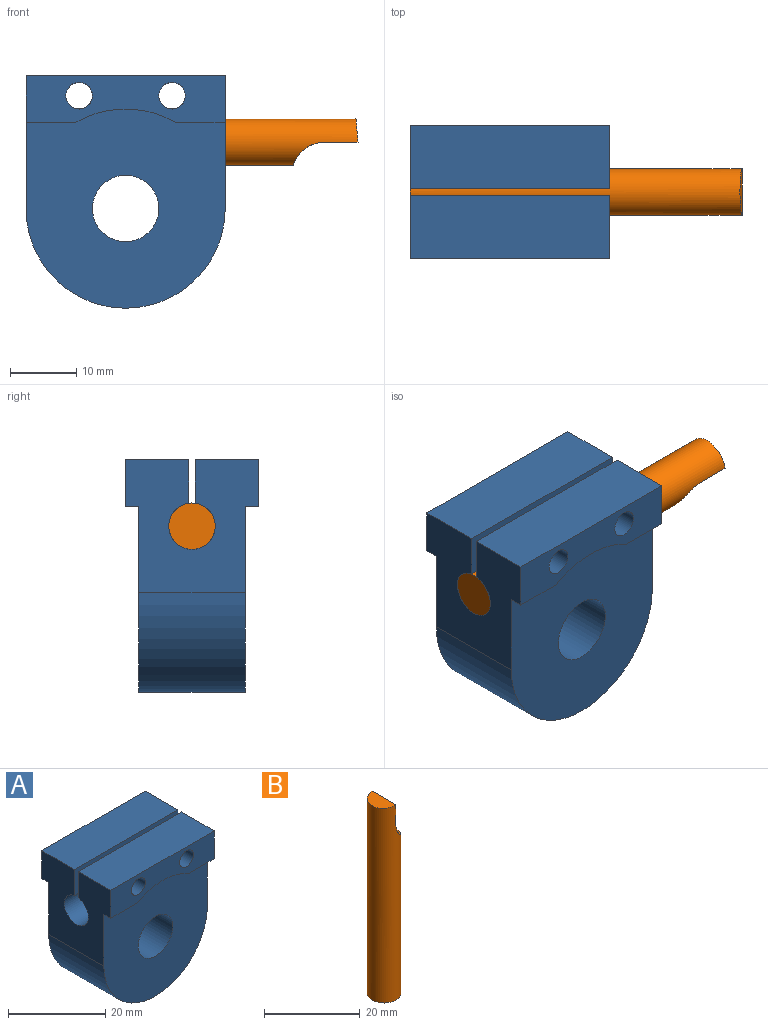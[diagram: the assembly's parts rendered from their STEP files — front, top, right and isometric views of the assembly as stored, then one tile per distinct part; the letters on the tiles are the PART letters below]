
ASSEMBLY  parts=2 mates=1
PART A: 23 faces, bbox 30x20x35 mm
  f0: cylinder r=5mm len=16mm, axis (0,1,0), area 502.7mm2, adj f18,f22
  f1: plane 20x20mm, normal (-1,0,0), area 303mm2, adj f3,f4,f5,f10,f11,f12,f13,f14
  f2: plane 20x20mm, normal (1,0,0), area 303mm2, adj f3,f4,f5,f10,f11,f12,f13,f14
  f3: cylinder r=15mm len=30mm, axis (0,1,0), area 754mm2, adj f1,f2,f18,f22
  f4: plane 30x7mm, normal (0,-1,0), area 164.6mm2, adj f1,f2,f5,f7,f9,f19,f20,f21
  f5: plane 30x9.5mm, normal (0,0,1), area 285mm2, adj f1,f2,f4,f14
  f6: cylinder r=2mm len=9.5mm, axis (0,1,0), area 119.4mm2, adj f11,f13
  f7: cylinder r=2mm len=9.5mm, axis (0,1,0), area 119.4mm2, adj f4,f14
  f8: cylinder r=2mm len=9.5mm, axis (0,1,0), area 119.4mm2, adj f11,f13
  f9: cylinder r=2mm len=9.5mm, axis (0,1,0), area 119.4mm2, adj f4,f14
  f10: plane 30x9.5mm, normal (0,0,1), area 285mm2, adj f1,f2,f11,f13
  f11: plane 30x7mm, normal (0,1,0), area 164.6mm2, adj f1,f2,f6,f8,f10,f15,f16,f17
  f12: cylinder r=3.5mm len=30mm, axis (1,0,0), area 629.6mm2, adj f1,f2,f13,f14
  f13: plane 30x6.54mm, normal (0,-1,0), area 170.9mm2, adj f1,f2,f6,f8,f10,f12
  f14: plane 30x6.54mm, normal (0,1,0), area 170.9mm2, adj f1,f2,f5,f7,f9,f12
  f15: plane 7.52x2mm, normal (0,0,-1), area 15mm2, adj f2,f11,f17,f18
  f16: plane 7.52x2mm, normal (0,0,-1), area 15mm2, adj f1,f11,f17,f18
  f17: cylinder r=15mm len=14.97mm, axis (0,1,0), area 31.3mm2, adj f11,f15,f16,f18
  f18: plane 30x30mm, normal (0,1,0), area 685.1mm2, adj f0,f1,f2,f3,f15,f16,f17
  f19: plane 7.52x2mm, normal (0,0,-1), area 15mm2, adj f1,f4,f21,f22
  f20: plane 7.52x2mm, normal (0,0,-1), area 15mm2, adj f2,f4,f21,f22
  f21: cylinder r=15mm len=14.97mm, axis (0,-1,0), area 31.3mm2, adj f4,f19,f20,f22
  f22: plane 30x30mm, normal (0,-1,0), area 685.1mm2, adj f0,f1,f2,f3,f19,f20,f21
PART B: 5 faces, bbox 7x7x50 mm
  f0: cylinder r=3.5mm len=50mm, axis (0,0,1), area 999.7mm2, adj f1,f2,f3,f4
  f1: plane 7x7mm, normal (0,0,-1), area 38.5mm2, adj f0
  f2: plane 7x5.3mm, normal (1,0,0), area 37.1mm2, adj f0,f3,f4
  f3: cylinder r=5mm len=7mm, axis (0,-1,0), area 36.1mm2, adj f0,f2
  f4: plane 7x3.5mm, normal (-0.09,0,1), area 19.3mm2, adj f0,f2
PLACE A t=(3.1,33.66,8.83)mm
PLACE B rot(axis=(0,1,0),90deg) t=(38.1,23.66,18.83)mm
MATE fastened B.f0 <-> A.f12  axis (-1,0,0) through (-11.9,23.66,18.83)mm
